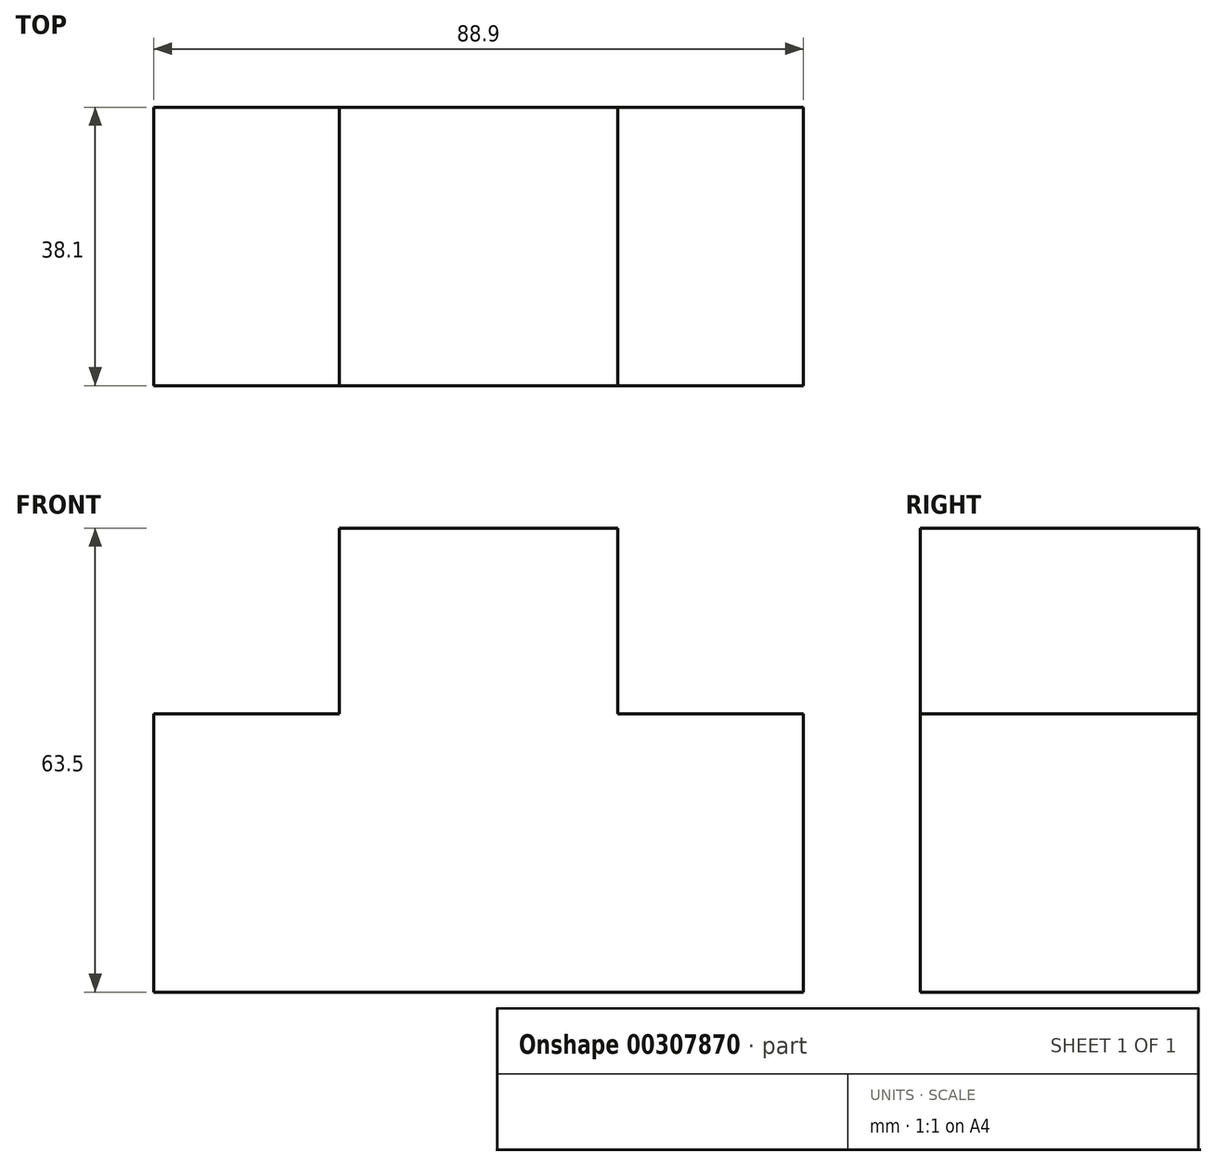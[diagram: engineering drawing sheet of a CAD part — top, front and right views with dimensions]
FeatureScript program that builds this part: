
annotation { "Feature Type Name" : "Feature", "Feature Type Description" : "" }
export const myFeature = defineFeature(function(context is Context, id is Id, definition is map)
    precondition{}
    {
        {
            var Q0;
            Q0=qCreatedBy(makeId("Front.planeOp"),FACE);
            var sketch = newSketch(context, id + "F0", { "sketchPlane" : qUnion([Q0])});
            skLineSegment(sketch, "E0", {"start": v(-41.6, -39.68) * mm, "end": v(47.3, -39.68) * mm});
            skLineSegment(sketch, "E1", {"start": v(47.3, -39.68) * mm, "end": v(47.3, -1.58) * mm});
            skLineSegment(sketch, "E2", {"start": v(47.3, -1.58) * mm, "end": v(21.9, -1.58) * mm});
            skLineSegment(sketch, "E3", {"start": v(21.9, -1.58) * mm, "end": v(21.9, 23.82) * mm});
            skLineSegment(sketch, "E4", {"start": v(21.9, 23.82) * mm, "end": v(-16.2, 23.82) * mm});
            skLineSegment(sketch, "E5", {"start": v(-16.2, 23.82) * mm, "end": v(-16.2, -1.58) * mm});
            skLineSegment(sketch, "E6", {"start": v(-16.2, -1.58) * mm, "end": v(-41.6, -1.58) * mm});
            skLineSegment(sketch, "E7", {"start": v(-41.6, -1.58) * mm, "end": v(-41.6, -39.68) * mm});
            skSolve(sketch);
        }
        {
            var Q0;
            Q0=makeQuery(id+"F0.imprint","IMPRINT",FACE,{"disambiguationData":[TD([[makeQuery(id+"F0.imprint","IMPRINT",EDGE,{"derivedFrom":sQuery(id+"F0.wireOp",EDGE,"E0")}),1.0]])]});
            extrude(context, id + "F1", {"entities" : qUnion([Q0]), "depth" : 38.1 * mm});
        }
    });
